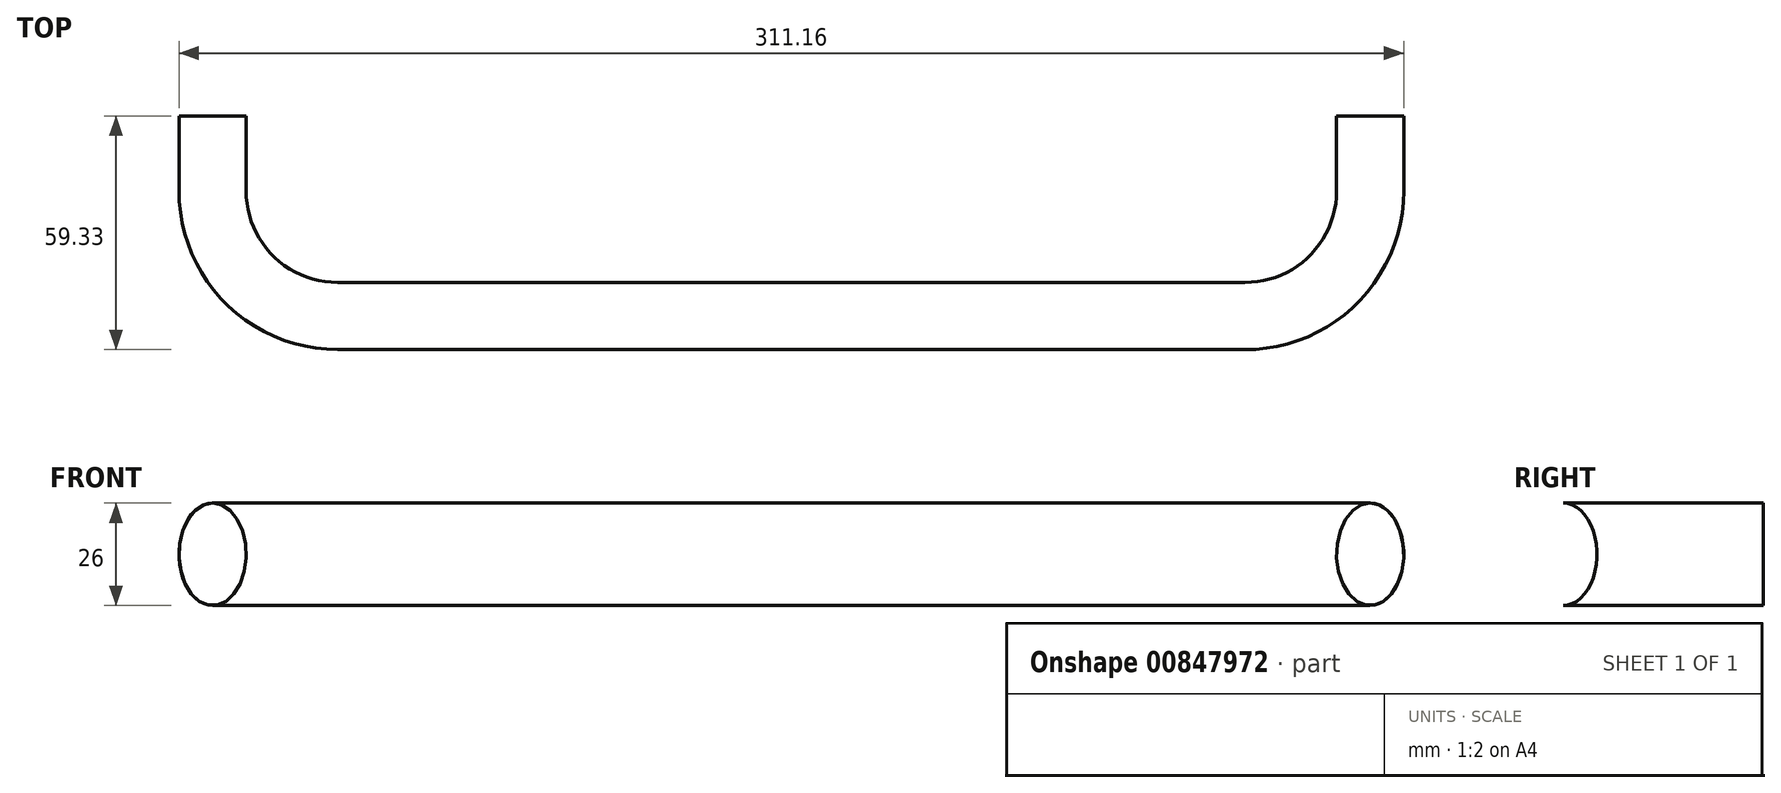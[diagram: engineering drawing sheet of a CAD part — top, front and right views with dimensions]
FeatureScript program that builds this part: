
annotation { "Feature Type Name" : "Feature", "Feature Type Description" : "" }
export const myFeature = defineFeature(function(context is Context, id is Id, definition is map)
    precondition{}
    {
        {
            var Q0;
            Q0=qCreatedBy(makeId("Front.planeOp"),FACE);
            var sketch = newSketch(context, id + "F0", { "sketchPlane" : qUnion([Q0])});
            skEllipse(sketch, "E0", {"center": v(147.04, 0) * mm, "majorRadius": 13 * mm, "minorRadius": 8.53 * mm, "majorAxis": v(0, 1)});
            skLineSegment(sketch, "E1", {"start": v(138.5, 0) * mm, "end": v(155.58, 0) * mm, "construction": true});
            skEllipse(sketch, "E2.MirrorC", {"center": v(-147.04, 0) * mm, "majorRadius": 13 * mm, "minorRadius": 8.53 * mm, "majorAxis": v(0, 1)});
            skSolve(sketch);
        }
        {
            var Q0;
            Q0=qCreatedBy(makeId("Top.planeOp"),FACE);
            var sketch = newSketch(context, id + "F1", { "sketchPlane" : qUnion([Q0])});
            skLineSegment(sketch, "E3", {"start": v(147.04, 0) * mm, "end": v(147.04, -19.05) * mm});
            skLineSegment(sketch, "E4", {"start": v(115.3, -50.8) * mm, "end": v(-115.3, -50.8) * mm});
            skLineSegment(sketch, "E5", {"start": v(-147.04, -19.05) * mm, "end": v(-147.04, 0) * mm});
            skPoint(sketch, "E6.visualSharp", {"position": v(147.04, -50.8) * mm});
            skArc(sketch, "E6.filletArc", {"start": v(115.3, -50.8) * mm, "mid": v(137.74, -41.5) * mm, "end": v(147.04, -19.05) * mm});
            skPoint(sketch, "E7.visualSharp", {"position": v(-147.04, -50.8) * mm});
            skArc(sketch, "E7.filletArc", {"start": v(-147.04, -19.05) * mm, "mid": v(-137.74, -41.5) * mm, "end": v(-115.3, -50.8) * mm});
            skSolve(sketch);
        }
        {
            var Q0;
            Q0=makeQuery(id+"F0.imprint","IMPRINT",FACE,{"disambiguationData":[TD([[makeQuery(id+"F0.imprint","IMPRINT",EDGE,{"derivedFrom":sQuery(id+"F0.wireOp",EDGE,"E0")}),1.0]])]});
            var Q1;
            Q1=sQuery(id+"F1.wireOp",EDGE,"E3");
            var Q2;
            Q2=sQuery(id+"F1.wireOp",EDGE,"E6.filletArc");
            var Q3;
            Q3=sQuery(id+"F1.wireOp",EDGE,"E4");
            var Q4;
            Q4=sQuery(id+"F1.wireOp",EDGE,"E7.filletArc");
            var Q5;
            Q5=sQuery(id+"F1.wireOp",EDGE,"E5");
            sweep(context, id + "F2", {"profiles" : qUnion([Q0]), "path" : qUnion([Q1, Q2, Q3, Q4, Q5])});
        }
    });
